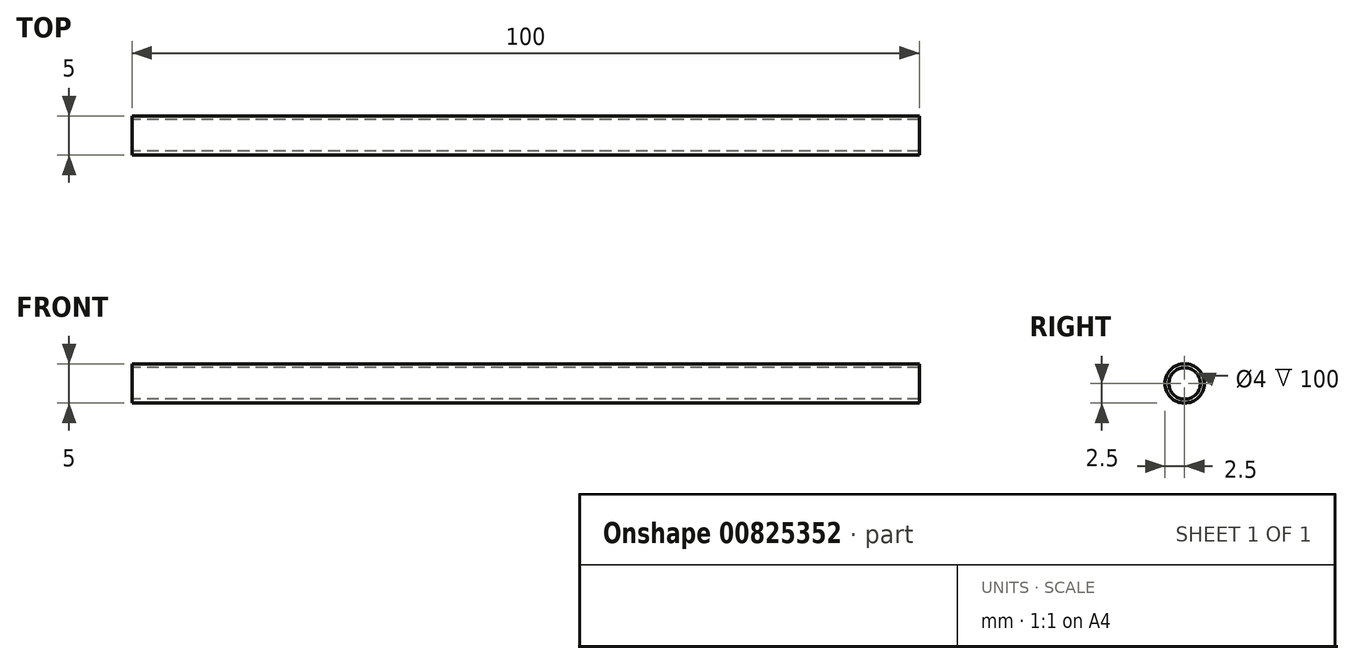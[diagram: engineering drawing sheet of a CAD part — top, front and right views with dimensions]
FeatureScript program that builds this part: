
annotation { "Feature Type Name" : "Feature", "Feature Type Description" : "" }
export const myFeature = defineFeature(function(context is Context, id is Id, definition is map)
    precondition{}
    {
        {
            var Q0;
            Q0=qCreatedBy(makeId("Right.planeOp"),FACE);
            var sketch = newSketch(context, id + "F0", { "sketchPlane" : qUnion([Q0])});
            skCircle(sketch, "E0", {"center": v(0, 0) * mm, "radius": 2.5 * mm});
            skCircle(sketch, "E1", {"center": v(0, 0) * mm, "radius": 2 * mm});
            skSolve(sketch);
        }
        {
            var Q0;
            Q0 = qSketchRegion(id + "F0", true);
            extrude(context, id + "F1", {"entities" : qUnion([Q0]), "depth" : 100 * mm, "offsetDistance" : 25 * mm});
        }
    });
